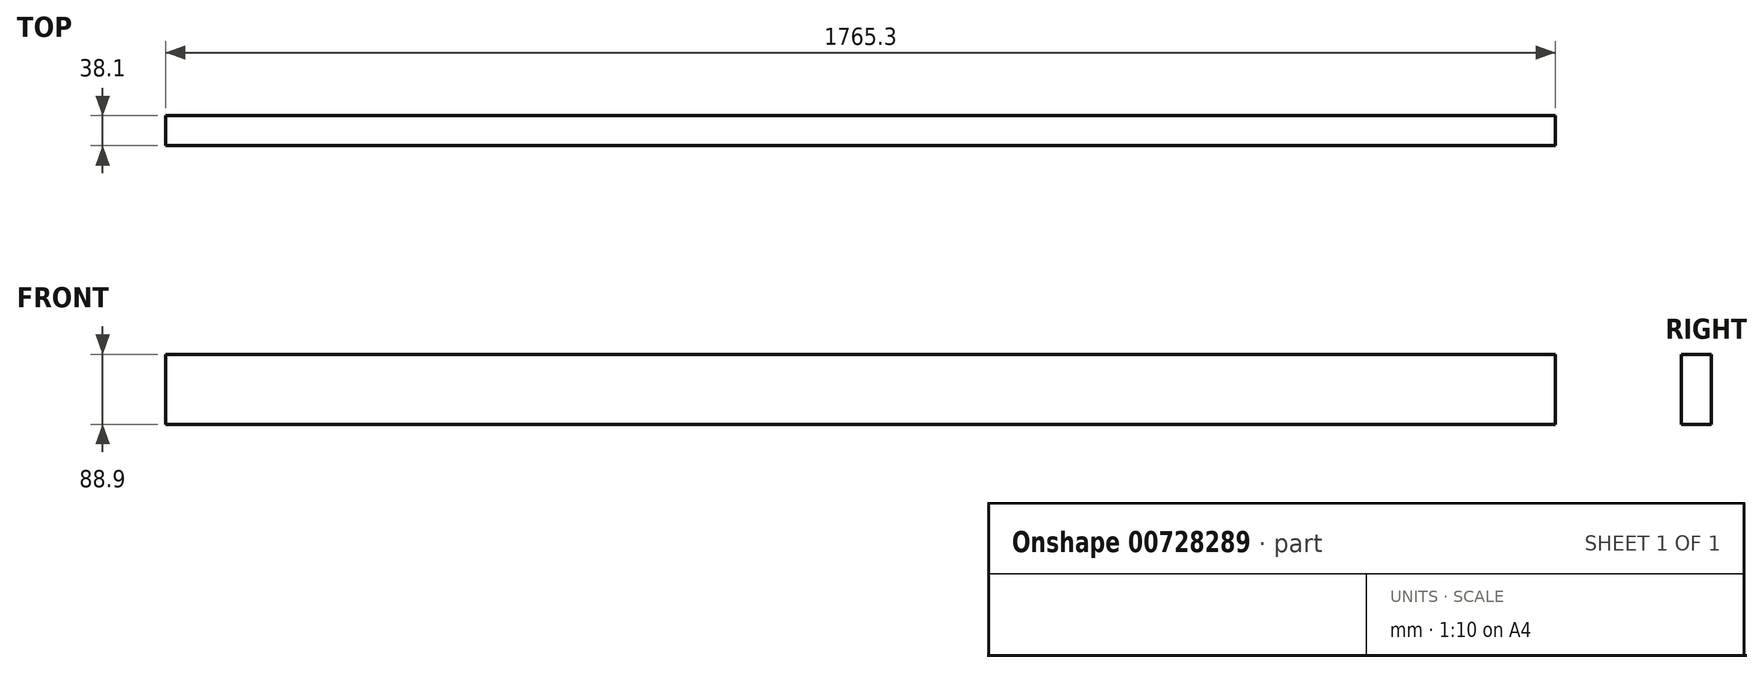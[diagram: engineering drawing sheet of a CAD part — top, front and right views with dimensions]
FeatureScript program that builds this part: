
annotation { "Feature Type Name" : "Feature", "Feature Type Description" : "" }
export const myFeature = defineFeature(function(context is Context, id is Id, definition is map)
    precondition{}
    {
        {
            var Q0;
            Q0=qCreatedBy(makeId("Front.planeOp"),FACE);
            var sketch = newSketch(context, id + "F0", { "sketchPlane" : qUnion([Q0])});
            skLineSegment(sketch, "E0.bottom", {"start": v(-882.65, -44.45) * mm, "end": v(882.65, -44.45) * mm});
            skLineSegment(sketch, "E0.top", {"start": v(-882.65, 44.45) * mm, "end": v(882.65, 44.45) * mm});
            skLineSegment(sketch, "E0.left", {"start": v(-882.65, -44.45) * mm, "end": v(-882.65, 44.45) * mm});
            skLineSegment(sketch, "E0.right", {"start": v(882.65, -44.45) * mm, "end": v(882.65, 44.45) * mm});
            skPoint(sketch, "E0.middle", {"position": v(0, 0) * mm});
            skSolve(sketch);
        }
        {
            var Q0;
            Q0=qSketchRegion(id+"F0",true);
            extrude(context, id + "F1", {"entities" : qUnion([Q0]), "depth" : 38.1 * mm, "offsetDistance" : 25.4 * mm});
        }
    });
